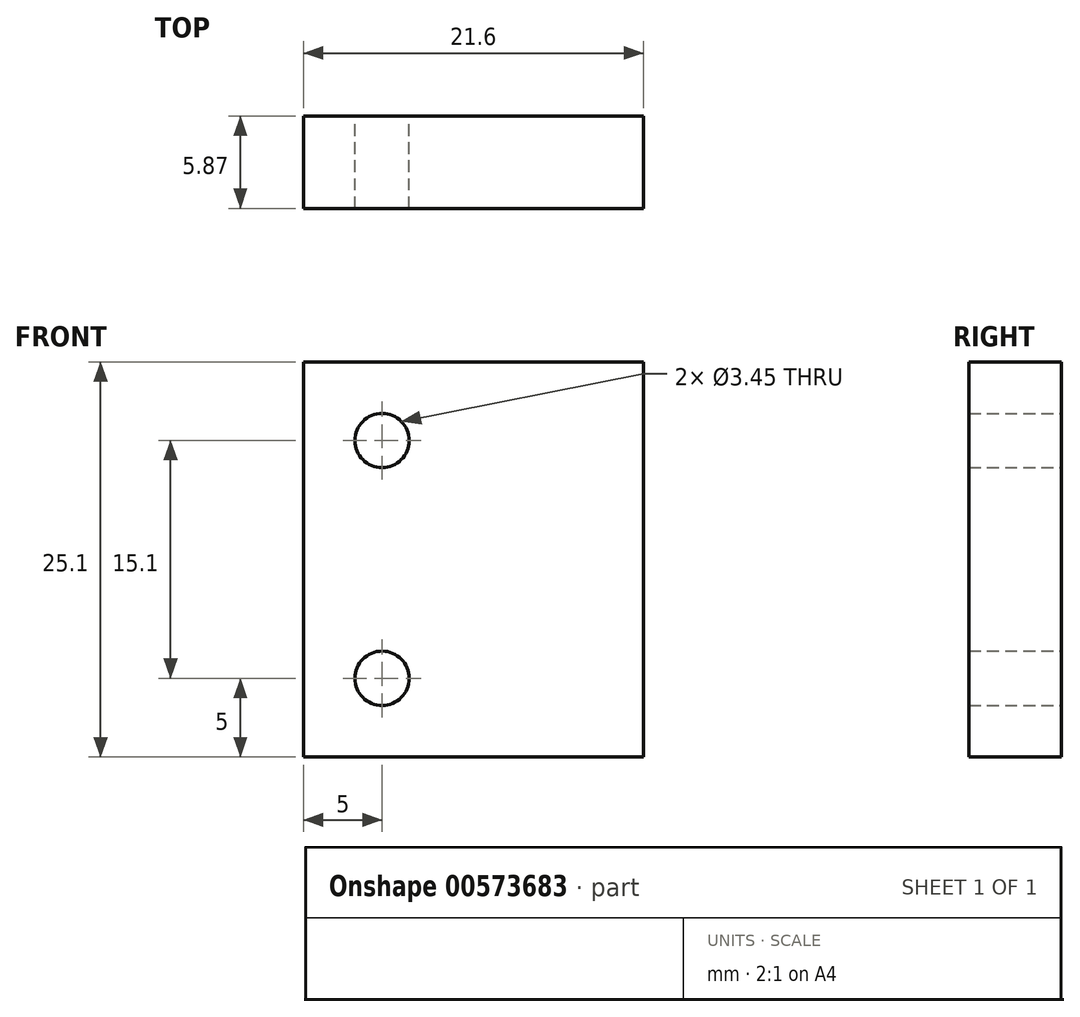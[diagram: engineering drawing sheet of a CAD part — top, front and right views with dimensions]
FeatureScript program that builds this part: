
annotation { "Feature Type Name" : "Feature", "Feature Type Description" : "" }
export const myFeature = defineFeature(function(context is Context, id is Id, definition is map)
    precondition{}
    {
        {
            var Q0;
            Q0=qCreatedBy(makeId("Front.planeOp"),FACE);
            var sketch = newSketch(context, id + "F0", { "sketchPlane" : qUnion([Q0])});
            skLineSegment(sketch, "E0.bottom", {"start": v(0, 0) * mm, "end": v(21.6, 0) * mm});
            skLineSegment(sketch, "E0.top", {"start": v(0, 25.1) * mm, "end": v(21.6, 25.1) * mm});
            skLineSegment(sketch, "E0.left", {"start": v(0, 0) * mm, "end": v(0, 25.1) * mm});
            skLineSegment(sketch, "E0.right", {"start": v(21.6, 0) * mm, "end": v(21.6, 25.1) * mm});
            skLineSegment(sketch, "E1", {"start": v(5, 0) * mm, "end": v(5, 25.1) * mm, "construction": true});
            skCircle(sketch, "E2", {"center": v(5, 5) * mm, "radius": 1.73 * mm});
            skCircle(sketch, "E3", {"center": v(5, 20.1) * mm, "radius": 1.73 * mm});
            skSolve(sketch);
        }
        {
            var Q0;
            Q0 = qSketchRegion(id + "F0", true);
            extrude(context, id + "F1", {"entities" : qUnion([Q0]), "depth" : 5.87 * mm, "offsetDistance" : 25 * mm});
        }
    });
